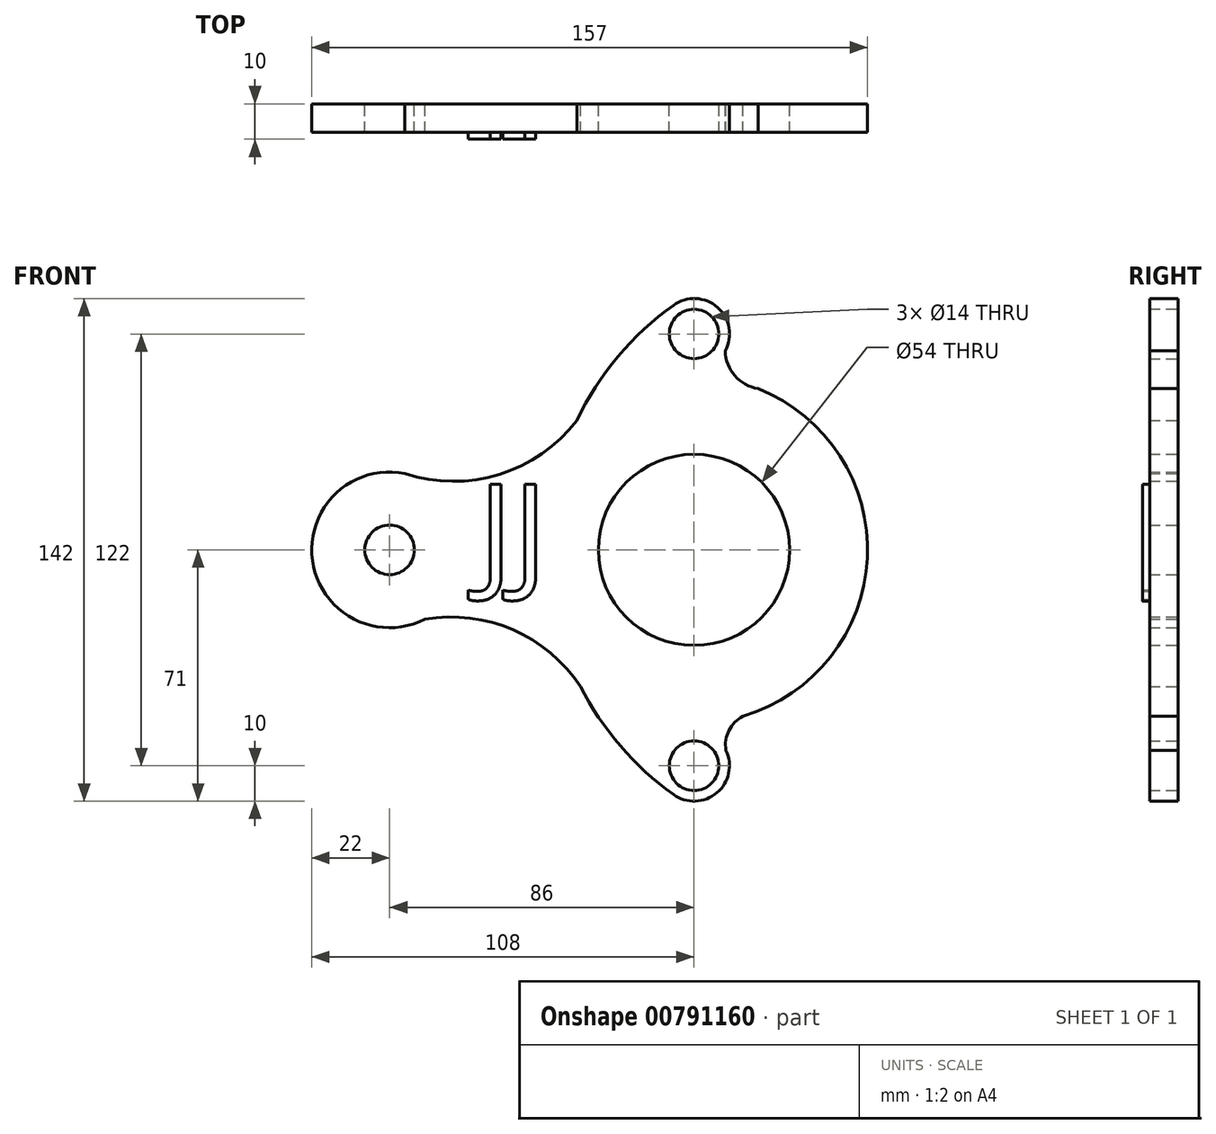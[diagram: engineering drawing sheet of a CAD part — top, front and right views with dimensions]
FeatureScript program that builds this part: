
annotation { "Feature Type Name" : "Feature", "Feature Type Description" : "" }
export const myFeature = defineFeature(function(context is Context, id is Id, definition is map)
    precondition{}
    {
        {
            var Q0;
            Q0=qCreatedBy(makeId("Front.planeOp"),FACE);
            var sketch = newSketch(context, id + "F0", { "sketchPlane" : qUnion([Q0])});
            skCircle(sketch, "E0", {"center": v(0, 0) * mm, "radius": 27 * mm});
            skLineSegment(sketch, "E1", {"start": v(0, 0) * mm, "end": v(-86, 0) * mm});
            skLineSegment(sketch, "E2", {"start": v(0, 0) * mm, "end": v(0, -61) * mm});
            skLineSegment(sketch, "E3", {"start": v(0, 0) * mm, "end": v(0, 61) * mm});
            skArc(sketch, "E4", {"start": v(-78.28, 20.6) * mm, "mid": v(-107.96, -1.26) * mm, "end": v(-75.98, -19.59) * mm});
            skCircle(sketch, "E5", {"center": v(-86, 0) * mm, "radius": 7 * mm});
            skArc(sketch, "E6", {"start": v(8.79, 56.23) * mm, "mid": v(6.62, 68.5) * mm, "end": v(-5.82, 69.13) * mm});
            skCircle(sketch, "E7", {"center": v(0, 61) * mm, "radius": 7 * mm});
            skArc(sketch, "E8", {"start": v(-5.82, -69.13) * mm, "mid": v(6.44, -68.65) * mm, "end": v(9, -56.65) * mm});
            skCircle(sketch, "E9", {"center": v(0, -61) * mm, "radius": 7 * mm});
            skArc(sketch, "E10", {"start": v(-5.82, 69.13) * mm, "mid": v(-21.51, 54.6) * mm, "end": v(-33.08, 36.6) * mm});
            skArc(sketch, "E11", {"start": v(-81.67, 21.57) * mm, "mid": v(-54.97, 21.32) * mm, "end": v(-33.08, 36.6) * mm});
            skArc(sketch, "E12", {"start": v(-32.1, -38.59) * mm, "mid": v(-51.21, -22.56) * mm, "end": v(-75.98, -19.59) * mm});
            skArc(sketch, "E13", {"start": v(8.79, 56.23) * mm, "mid": v(11.54, 49.2) * mm, "end": v(18.12, 45.52) * mm});
            skArc(sketch, "E14", {"start": v(13.85, -47) * mm, "mid": v(9.84, -51.03) * mm, "end": v(9, -56.65) * mm});
            skArc(sketch, "E15.trimOffspring", {"start": v(13.85, -47) * mm, "mid": v(49, -0.32) * mm, "end": v(14.47, 46.81) * mm});
            skArc(sketch, "E16.trimOffspring", {"start": v(-32.1, -38.59) * mm, "mid": v(-20.8, -55.44) * mm, "end": v(-5.82, -69.13) * mm});
            skSolve(sketch);
        }
        {
            var Q0;
            Q0=makeQuery(id+"F0.imprint","IMPRINT",FACE,{"disambiguationData":[TD([[makeQuery(id+"F0.imprint","IMPRINT",EDGE,{"derivedFrom":sQuery(id+"F0.wireOp",EDGE,"E5")}),-1.0]])]});
            extrude(context, id + "F1", {"entities" : qUnion([Q0]), "depth" : 8 * mm, "offsetDistance" : 25 * mm});
        }
        {
            var Q0;
            Q0=makeQuery(id+"F1.opExtrude","CAP_FACE",FACE,{"disambiguationData":[OSD([sQuery(id+"F0.wireOp",EDGE,"E0"),sQuery(id+"F0.wireOp",EDGE,"E4"),sQuery(id+"F0.wireOp",EDGE,"E5"),sQuery(id+"F0.wireOp",EDGE,"E6"),sQuery(id+"F0.wireOp",EDGE,"E7"),sQuery(id+"F0.wireOp",EDGE,"E8"),sQuery(id+"F0.wireOp",EDGE,"E9"),sQuery(id+"F0.wireOp",EDGE,"E10"),sQuery(id+"F0.wireOp",EDGE,"E11"),sQuery(id+"F0.wireOp",EDGE,"E12"),sQuery(id+"F0.wireOp",EDGE,"E13"),sQuery(id+"F0.wireOp",EDGE,"E14"),sQuery(id+"F0.wireOp",EDGE,"E15.trimOffspring"),sQuery(id+"F0.wireOp",EDGE,"E16.trimOffspring")])],"isStart":false});
            var sketch = newSketch(context, id + "F2", { "sketchPlane" : qUnion([Q0])});
            skText(sketch, "E17", { "text": "JJ", "fontName": "OpenSans-Regular.ttf"});
            const initialGuessF2  = {"E17": [-0.06092, -0.00757, 1, 0, 0.02634]};
            skSetInitialGuess(sketch, initialGuessF2);
            skSolve(sketch);
        }
        {
            var Q0;
            Q0 = qSketchRegion(id + "F2", true);
            extrude(context, id + "F3", {"entities" : qUnion([Q0]), "operationType" : NewBodyOperationType.ADD, "depth" : 2 * mm, "offsetDistance" : 25 * mm});
        }
    });
